# Revit family: Информационный стенд «Борд» Арт 14041
name_source: partatom
category: Антураж
revit_build: Autodesk Revit 2018 (Build: 20180423_1000(x64)
units: mm (PartAtom-declared; Revit-internal decimal feet)

## family parameters
Всегда вертикально = Да
Источник визуального образа = Геометрия семейства
На основе рабочей плоскости = Нет
Общий = Нет
При загрузке вырезать с полостями = Нет
Точка расчета площади = Нет

## types (2) — shared parameters
URL = https://hobbyka.ru
Группа модели = Стенды и указатели
Изготовитель = ООО «Хоббика»
Материал изделия = Дерево

## per-type parameters (varying)
| type | Большой щит | Высота | Длина | Изображение типоразмера | Малый щит | Описание | Ширина |
| Информационный стенд «Борд» Большой щит | Да | 2380 мм | 1800 мм | Информационный стенд «Борд» большой щит.png | Нет | Информационный стенд «Борд» Модель «большой щит» | 500 мм |
| Информационный стенд «Борд» Малый щит | Нет | 1035 мм | 1200 мм | Информационный стенд «Борд» малый щит.png | Да | Информационный стенд «Борд» Модель «малый щит» | 825 мм |
